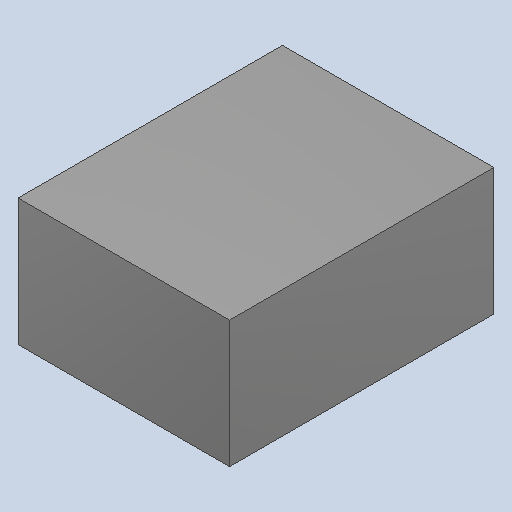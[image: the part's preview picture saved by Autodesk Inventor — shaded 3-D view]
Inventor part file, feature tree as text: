
AUTODESK INVENTOR PART (.ipt)
format: ipt  version: 2022.1 (Build 261234000, 234)  size: 87,040 bytes
history: imported  units: mm
features: imported_body x1
ambient origin geometry x8: Origin, YZ Plane, XZ Plane, XY Plane, X Axis, Y Axis, Z Axis, Center Point
bodies: Solid1 (imported_parasolid)
feature tree (1):
  imported_body  NMx_Import_Brep_tag  [imported B-rep: ~6 faces, bbox_mm=[2.0, 1.2, 2.5]]
